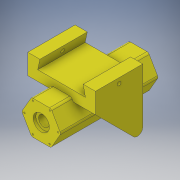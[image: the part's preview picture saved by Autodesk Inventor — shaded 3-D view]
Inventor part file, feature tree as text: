
AUTODESK INVENTOR PART (.ipt)
format: ipt  version: 2016 (Build 200138000, 138)  size: 231,936 bytes
history: native  units: in
note: dims shown in document units (in); Inventor stores cm internally (conversion verified against a paired STEP export)
features: extrude x7, sketch x7, fillet x2
ambient origin geometry x8: Origin, YZ Plane, XZ Plane, XY Plane, X Axis, Y Axis, Z Axis, Center Point
bodies: Solid1 (feature_tree)
feature tree (16):
  extrude  "Extrusion1"  Depth=2.8346in TaperAngle=0.0deg
  extrude  "Extrusion2"  Depth=0.0787in TaperAngle=0.0deg
  extrude  "Extrusion3"  Depth=0.0407in
  extrude  "Extrusion4"  Depth=0.0787in
  fillet  "Fillet1"  Radius=0.1575in
  fillet  "Fillet2"  Radius=0.5906in
  extrude  "Extrusion5"  Depth=1.378in
  extrude  "Extrusion6"  Depth=0.1575in
  extrude  "Extrusion8"  Depth=0.9843in
  sketch  "Sketch1"  dims[d2=0.315in d3=2.8346in d4=0.0in]
  sketch  "Sketch2"  dims[d5=0.4724in d6=0.0787in d7=0.0in]
  sketch  "Sketch3"  dims[d8=0.0407in d11=0.0407in]
  sketch  "Sketch4"  dims[d14=0.0787in d15=0.0787in d16=0.1575in d17=0.0in d20=0.5906in]
  sketch  "Sketch5"  dims[d21=1.378in d22=1.378in]
  sketch  "Sketch6"  dims[d23=1.9685in d24=0.0in d25=0.1575in]
  sketch  "Sketch8"  dims[d26=0.0787in d27=0.9843in d29=0.9843in d30=0.0407in d31=0.0407in d32=0.0407in d33=0.0407in d35=0.3543in d37=0.536in d38=0.7009in d39=19.685in d40=0.0in d41=0.689in d42=0.1102in d43=2.7559in d44=0.0in d47=0.8661in d48=0.9843in d49=45.0deg d50=2.7559in d51=0.0in]
